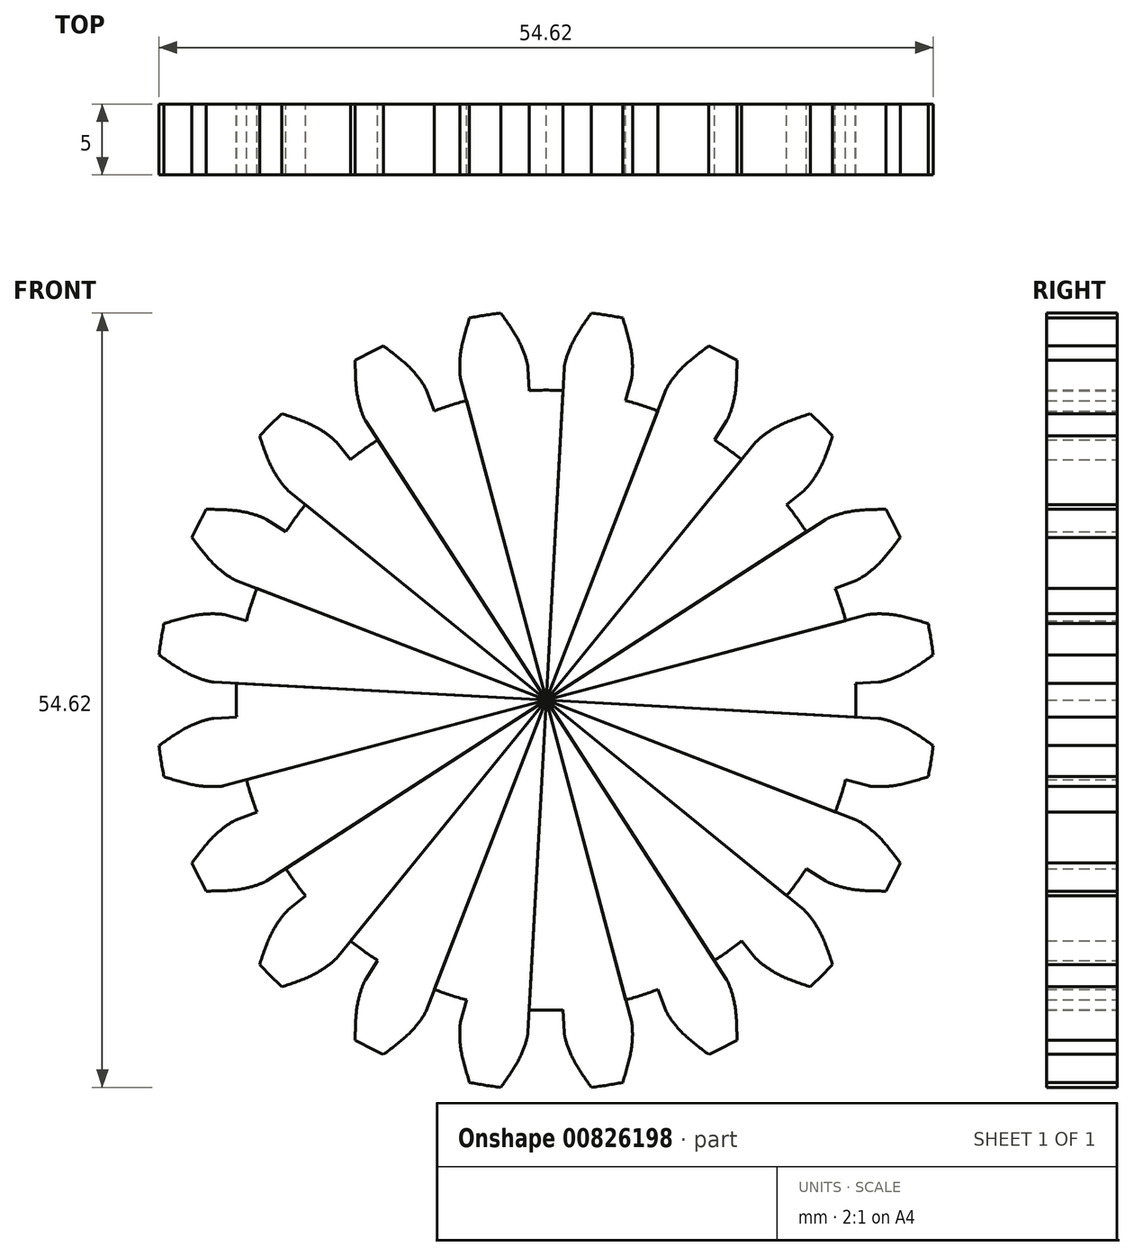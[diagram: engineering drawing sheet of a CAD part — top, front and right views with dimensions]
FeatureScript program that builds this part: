
annotation { "Feature Type Name" : "Feature", "Feature Type Description" : "" }
export const myFeature = defineFeature(function(context is Context, id is Id, definition is map)
    precondition{}
    {
        {
            assignVariable(context, id + "F0", {"name" : "T", "anyValue" : 20});
        }
        {
            var Q0;
            Q0=qCreatedBy(makeId("Front.planeOp"),FACE);
            var sketch = newSketch(context, id + "F1", { "sketchPlane" : qUnion([Q0])});
            skCircle(sketch, "E0", {"center": v(0, 0) * mm, "radius": 25 * mm});
            skCircle(sketch, "E1.0", {"center": v(0, 0) * mm, "radius": 27.5 * mm});
            skCircle(sketch, "E2.0", {"center": v(0, 0) * mm, "radius": 21.88 * mm});
            skLineSegment(sketch, "E3", {"start": v(-5.4, 26.96) * mm, "end": v(8.03, 22.08) * mm, "construction": true});
            skLineSegment(sketch, "E4", {"start": v(-31.54, 0) * mm, "end": v(33.12, 0) * mm, "construction": true});
            skLineSegment(sketch, "E5", {"start": v(0, 0) * mm, "end": v(0, 25) * mm, "construction": true});
            skPoint(sketch, "E6", {"position": v(0, 25) * mm});
            skArc(sketch, "E7", {"start": v(8.03, 22.08) * mm, "mid": v(-13.47, 19.24) * mm, "end": v(-23.5, 0) * mm});
            skLineSegment(sketch, "E8", {"start": v(-5.4, 26.96) * mm, "end": v(0, 0) * mm});
            skLineSegment(sketch, "E9", {"start": v(0, 0) * mm, "end": v(8.03, 22.08) * mm});
            skLineSegment(sketch, "E10", {"start": v(0, 0) * mm, "end": v(-6.03, 22.7) * mm});
            skLineSegment(sketch, "E11", {"start": v(0, 0) * mm, "end": v(4.6, 23.04) * mm});
            skLineSegment(sketch, "E12", {"start": v(1.05, 23.47) * mm, "end": v(0, 0) * mm});
            skLineSegment(sketch, "E13", {"start": v(-2.52, 23.36) * mm, "end": v(0, 0) * mm});
            skLineSegment(sketch, "E14", {"start": v(-2.52, 23.36) * mm, "end": v(-6.07, 22.97) * mm, "construction": true});
            skLineSegment(sketch, "E15", {"start": v(4.6, 23.04) * mm, "end": v(-5.92, 25.14) * mm, "construction": true});
            skLineSegment(sketch, "E16", {"start": v(1.05, 23.47) * mm, "end": v(-6.1, 23.79) * mm, "construction": true});
            skFitSpline(sketch, "E17", {"points": [v(-5.4, 26.96) * mm, v(-5.92, 25.14) * mm, v(-6.1, 23.79) * mm, v(-6.07, 22.97) * mm, v(-6.03, 22.7) * mm], "startDerivative": vector(-1.71, -5.42) * mm, "endDerivative": vector(0.47, -1.75) * mm});
            skLineSegment(sketch, "E18", {"start": v(0, 0) * mm, "end": v(-6.79, 42.85) * mm, "construction": true});
            skFitSpline(sketch, "E19.MirrorCS", {"points": [v(-3.2, 27.31) * mm, v(-2.14, 25.73) * mm, v(-1.56, 24.5) * mm, v(-1.32, 23.73) * mm, v(-1.28, 23.46) * mm], "startDerivative": vector(3.3, -4.62) * mm, "endDerivative": vector(0.1, -1.81) * mm});
            skLineSegment(sketch, "E20.MirrorCS", {"start": v(0, 0) * mm, "end": v(-1.28, 23.46) * mm});
            skFitSpline(sketch, "E21.MirrorCS", {"points": [v(3.2, 27.31) * mm, v(2.14, 25.73) * mm, v(1.56, 24.5) * mm, v(1.32, 23.73) * mm, v(1.28, 23.46) * mm], "startDerivative": vector(-3.3, -4.62) * mm, "endDerivative": vector(-0.1, -1.81) * mm});
            skLineSegment(sketch, "E22.MirrorCS", {"start": v(0, 0) * mm, "end": v(1.28, 23.46) * mm});
            skSolve(sketch);
        }
        {
            var Q0;
            Q0=qCreatedBy(makeId("Right.planeOp"),FACE);
            var sketch = newSketch(context, id + "F2", { "sketchPlane" : qUnion([Q0])});
            skLineSegment(sketch, "E23", {"start": v(-19.84, 0) * mm, "end": v(24.08, 0) * mm, "construction": true});
            skSolve(sketch);
        }
        {
            var Q0;
            {var subQ0=sQuery(id+"F1.wireOp",EDGE,"E19.MirrorCS");var subQ1=sQuery(id+"F1.wireOp",EDGE,"E0");var subQ2=makeQuery(id+"F1.imprint","INTERSECT",VERTEX,{"derivedFrom":[subQ1,subQ0]});Q0=makeQuery(id+"F1.imprint","IMPRINT",FACE,{"disambiguationData":[TD([[makeQuery(id+"F1.imprint","IMPRINT",EDGE,{"disambiguationData":[TD([[subQ2,-1.0]])],"derivedFrom":subQ1}),-1.0]])]});}
            var Q1;
            {var subQ0=sQuery(id+"F1.wireOp",EDGE,"E8");var subQ1=sQuery(id+"F1.wireOp",EDGE,"E0");var subQ2=makeQuery(id+"F1.imprint","INTERSECT",VERTEX,{"derivedFrom":[subQ1,subQ0]});Q1=makeQuery(id+"F1.imprint","IMPRINT",FACE,{"disambiguationData":[TD([[makeQuery(id+"F1.imprint","IMPRINT",EDGE,{"disambiguationData":[TD([[subQ2,-1.0]])],"derivedFrom":subQ1}),-1.0]])]});}
            var Q2;
            {var subQ0=sQuery(id+"F1.wireOp",EDGE,"E8");var subQ1=sQuery(id+"F1.wireOp",EDGE,"E0");var subQ2=makeQuery(id+"F1.imprint","INTERSECT",VERTEX,{"derivedFrom":[subQ1,subQ0]});Q2=makeQuery(id+"F1.imprint","IMPRINT",FACE,{"disambiguationData":[TD([[makeQuery(id+"F1.imprint","IMPRINT",EDGE,{"disambiguationData":[TD([[subQ2,-1.0]])],"derivedFrom":subQ1}),1.0]])]});}
            var Q3;
            {var subQ1=sQuery(id+"F1.wireOp",EDGE,"E0");var subQ5=sQuery(id+"F1.wireOp",EDGE,"E19.MirrorCS");var subQ6=makeQuery(id+"F1.imprint","INTERSECT",VERTEX,{"derivedFrom":[subQ1,subQ5]});Q3=makeQuery(id+"F1.imprint","IMPRINT",FACE,{"disambiguationData":[TD([[makeQuery(id+"F1.imprint","IMPRINT",EDGE,{"disambiguationData":[TD([[subQ6,-1.0]])],"derivedFrom":subQ1}),1.0]])]});}
            var Q4;
            {var subQ0=sQuery(id+"F1.wireOp",EDGE,"E20.MirrorCS");var subQ1=sQuery(id+"F1.wireOp",EDGE,"E2.0");var subQ2=makeQuery(id+"F1.imprint","INTERSECT",VERTEX,{"derivedFrom":[subQ1,subQ0]});Q4=makeQuery(id+"F1.imprint","IMPRINT",FACE,{"disambiguationData":[TD([[makeQuery(id+"F1.imprint","IMPRINT",EDGE,{"disambiguationData":[TD([[subQ2,-1.0]])],"derivedFrom":subQ1}),-1.0]])]});}
            var Q5;
            {var subQ0=sQuery(id+"F1.wireOp",EDGE,"E13");var subQ1=sQuery(id+"F1.wireOp",EDGE,"E2.0");var subQ2=makeQuery(id+"F1.imprint","INTERSECT",VERTEX,{"derivedFrom":[subQ1,subQ0]});Q5=makeQuery(id+"F1.imprint","IMPRINT",FACE,{"disambiguationData":[TD([[makeQuery(id+"F1.imprint","IMPRINT",EDGE,{"disambiguationData":[TD([[subQ2,-1.0]])],"derivedFrom":subQ1}),-1.0]])]});}
            var Q6;
            {var subQ0=sQuery(id+"F1.wireOp",EDGE,"E8");var subQ1=sQuery(id+"F1.wireOp",EDGE,"E2.0");var subQ2=makeQuery(id+"F1.imprint","INTERSECT",VERTEX,{"derivedFrom":[subQ1,subQ0]});Q6=makeQuery(id+"F1.imprint","IMPRINT",FACE,{"disambiguationData":[TD([[makeQuery(id+"F1.imprint","IMPRINT",EDGE,{"disambiguationData":[TD([[subQ2,-1.0]])],"derivedFrom":subQ1}),-1.0]])]});}
            var Q7;
            {var subQ0=sQuery(id+"F1.wireOp",EDGE,"E8");var subQ1=sQuery(id+"F1.wireOp",EDGE,"E2.0");var subQ2=makeQuery(id+"F1.imprint","INTERSECT",VERTEX,{"derivedFrom":[subQ1,subQ0]});Q7=makeQuery(id+"F1.imprint","IMPRINT",FACE,{"disambiguationData":[TD([[makeQuery(id+"F1.imprint","IMPRINT",EDGE,{"disambiguationData":[TD([[subQ2,-1.0]])],"derivedFrom":subQ1}),1.0]])]});}
            var Q8;
            {var subQ0=sQuery(id+"F1.wireOp",EDGE,"E13");var subQ1=sQuery(id+"F1.wireOp",EDGE,"E2.0");var subQ2=makeQuery(id+"F1.imprint","INTERSECT",VERTEX,{"derivedFrom":[subQ1,subQ0]});Q8=makeQuery(id+"F1.imprint","IMPRINT",FACE,{"disambiguationData":[TD([[makeQuery(id+"F1.imprint","IMPRINT",EDGE,{"disambiguationData":[TD([[subQ2,-1.0]])],"derivedFrom":subQ1}),1.0]])]});}
            var Q9;
            {var subQ0=sQuery(id+"F1.wireOp",EDGE,"E20.MirrorCS");var subQ1=sQuery(id+"F1.wireOp",EDGE,"E2.0");var subQ2=makeQuery(id+"F1.imprint","INTERSECT",VERTEX,{"derivedFrom":[subQ1,subQ0]});Q9=makeQuery(id+"F1.imprint","IMPRINT",FACE,{"disambiguationData":[TD([[makeQuery(id+"F1.imprint","IMPRINT",EDGE,{"disambiguationData":[TD([[subQ2,-1.0]])],"derivedFrom":subQ1}),1.0]])]});}
            var Q10;
            {var subQ0=sQuery(id+"F1.wireOp",EDGE,"E12");var subQ1=sQuery(id+"F1.wireOp",EDGE,"E2.0");var subQ2=makeQuery(id+"F1.imprint","INTERSECT",VERTEX,{"derivedFrom":[subQ1,subQ0]});Q10=makeQuery(id+"F1.imprint","IMPRINT",FACE,{"disambiguationData":[TD([[makeQuery(id+"F1.imprint","IMPRINT",EDGE,{"disambiguationData":[TD([[subQ2,-1.0]])],"derivedFrom":subQ1}),1.0]])]});}
            var Q11;
            {var subQ0=sQuery(id+"F1.wireOp",EDGE,"E22.MirrorCS");var subQ1=sQuery(id+"F1.wireOp",EDGE,"E2.0");var subQ2=makeQuery(id+"F1.imprint","INTERSECT",VERTEX,{"derivedFrom":[subQ1,subQ0]});Q11=makeQuery(id+"F1.imprint","IMPRINT",FACE,{"disambiguationData":[TD([[makeQuery(id+"F1.imprint","IMPRINT",EDGE,{"disambiguationData":[TD([[subQ2,-1.0]])],"derivedFrom":subQ1}),1.0]])]});}
            extrude(context, id + "F3", {"entities" : qUnion([Q0, Q1, Q2, Q3, Q4, Q5, Q6, Q7, Q8, Q9, Q10, Q11]), "depth" : 5 * mm, "offsetDistance" : 25 * mm});
        }
        {
            var Q0;
            Q0=makeQuery(id+"F3.opExtrude","SWEPT_BODY",BODY,{"disambiguationData":[OSD([sQuery(id+"F1.wireOp",EDGE,"E1.0"),sQuery(id+"F1.wireOp",EDGE,"E7"),sQuery(id+"F1.wireOp",EDGE,"E10"),sQuery(id+"F1.wireOp",EDGE,"E17"),sQuery(id+"F1.wireOp",EDGE,"E19.MirrorCS"),sQuery(id+"F1.wireOp",EDGE,"E22.MirrorCS")])]});
            var Q1;
            Q1=sQuery(id+"F2.wireOp",EDGE,"E23");
            circularPattern(context, id + "F4", {"entities" : qUnion([Q0]), "axis" : qUnion([Q1]), "angle" : 360 * degree, "instanceCount" : getVariable(context, 'T'), "equalSpace" : true});
        }
    });
